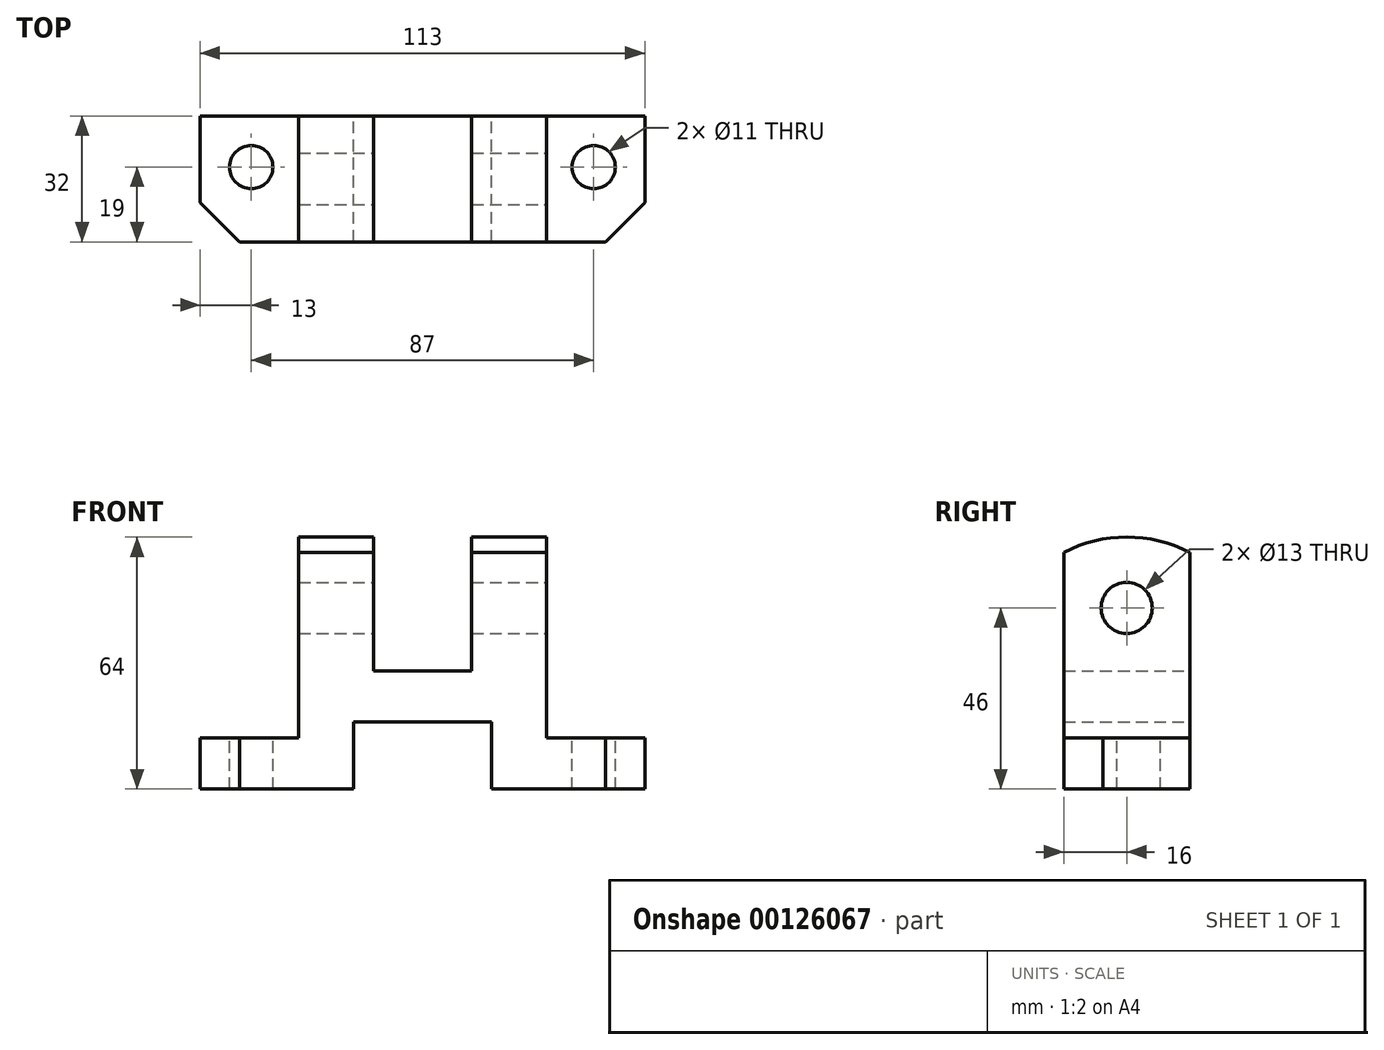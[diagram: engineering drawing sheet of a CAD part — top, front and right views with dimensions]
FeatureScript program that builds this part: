
annotation { "Feature Type Name" : "Feature", "Feature Type Description" : "" }
export const myFeature = defineFeature(function(context is Context, id is Id, definition is map)
    precondition{}
    {
        {
            var Q0;
            Q0=qCreatedBy(makeId("Front.planeOp"),FACE);
            var sketch = newSketch(context, id + "F0", { "sketchPlane" : qUnion([Q0])});
            skLineSegment(sketch, "E0.bottom", {"start": v(0, 0) * mm, "end": v(39, 0) * mm});
            skLineSegment(sketch, "E0.top", {"start": v(25, 64) * mm, "end": v(44, 64) * mm});
            skLineSegment(sketch, "E0.left", {"start": v(0, 0) * mm, "end": v(0, 13) * mm});
            skLineSegment(sketch, "E0.right", {"start": v(113, 0) * mm, "end": v(113, 13) * mm});
            skLineSegment(sketch, "E1.top", {"start": v(39, 17) * mm, "end": v(74, 17) * mm});
            skLineSegment(sketch, "E1.left", {"start": v(39, 0) * mm, "end": v(39, 17) * mm});
            skLineSegment(sketch, "E1.right", {"start": v(74, 0) * mm, "end": v(74, 17) * mm});
            skLineSegment(sketch, "E2.top", {"start": v(44, 30) * mm, "end": v(69, 30) * mm});
            skLineSegment(sketch, "E2.left", {"start": v(44, 64) * mm, "end": v(44, 30) * mm});
            skLineSegment(sketch, "E2.right", {"start": v(69, 64) * mm, "end": v(69, 30) * mm});
            skLineSegment(sketch, "E3.top", {"start": v(88, 13) * mm, "end": v(113, 13) * mm});
            skLineSegment(sketch, "E3.left", {"start": v(88, 64) * mm, "end": v(88, 13) * mm});
            skLineSegment(sketch, "E4.top", {"start": v(25, 13) * mm, "end": v(0, 13) * mm});
            skLineSegment(sketch, "E4.left", {"start": v(25, 64) * mm, "end": v(25, 13) * mm});
            skLineSegment(sketch, "E5.trimOffspring", {"start": v(69, 64) * mm, "end": v(88, 64) * mm});
            skLineSegment(sketch, "E6.trimOffspring", {"start": v(74, 0) * mm, "end": v(113, 0) * mm});
            skSolve(sketch);
        }
        {
            var Q0;
            Q0=makeQuery(id+"F0.imprint","IMPRINT",FACE,{"disambiguationData":[TD([[makeQuery(id+"F0.imprint","IMPRINT",EDGE,{"derivedFrom":sQuery(id+"F0.wireOp",EDGE,"E0.bottom")}),1.0]])]});
            extrude(context, id + "F1", {"entities" : qUnion([Q0]), "endBound" : BoundingType.SYMMETRIC, "depth" : 32 * mm});
        }
        {
            var Q0;
            Q0=makeQuery(id+"F1.opExtrude","SWEPT_FACE",FACE,{"disambiguationData":[OSD([sQuery(id+"F0.wireOp",EDGE,"E3.top")])]});
            var sketch = newSketch(context, id + "F2", { "sketchPlane" : qUnion([Q0])});
            skCircle(sketch, "E7", {"center": v(100, 3) * mm, "radius": 5.5 * mm});
            skCircle(sketch, "E8", {"center": v(13, 3) * mm, "radius": 5.5 * mm});
            skSolve(sketch);
        }
        {
            var Q0;
            Q0=makeQuery(id+"F2.imprint","IMPRINT",FACE,{"disambiguationData":[TD([[makeQuery(id+"F2.imprint","IMPRINT",EDGE,{"derivedFrom":sQuery(id+"F2.wireOp",EDGE,"E7")}),1.0]])]});
            var Q1;
            Q1=makeQuery(id+"F2.imprint","IMPRINT",FACE,{"disambiguationData":[TD([[makeQuery(id+"F2.imprint","IMPRINT",EDGE,{"derivedFrom":sQuery(id+"F2.wireOp",EDGE,"E8")}),1.0]])]});
            extrude(context, id + "F3", {"entities" : qUnion([Q0, Q1]), "operationType" : NewBodyOperationType.REMOVE, "endBound" : BoundingType.THROUGH_ALL, "oppositeDirection" : true, "depth" : 25 * mm});
        }
        {
            var Q0;
            Q0=makeQuery(id+"F1.opExtrude","CAP_EDGE",EDGE,{"disambiguationData":[OSD([sQuery(id+"F0.wireOp",EDGE,"E0.left")])],"isStart":false});
            var Q1;
            Q1=makeQuery(id+"F1.opExtrude","CAP_EDGE",EDGE,{"disambiguationData":[OSD([sQuery(id+"F0.wireOp",EDGE,"E0.right")])],"isStart":false});
            chamfer(context, id + "F4", {"entities" : qUnion([Q0, Q1]), "chamferType" : ChamferType.OFFSET_ANGLE, "width" : 10 * mm, "oppositeDirection" : false, "angle" : 45 * degree, "tangentPropagation" : true});
        }
        {
            var Q0;
            Q0=makeQuery(id+"F1.opExtrude","SWEPT_FACE",FACE,{"disambiguationData":[OSD([sQuery(id+"F0.wireOp",EDGE,"E3.left")])]});
            var sketch = newSketch(context, id + "F5", { "sketchPlane" : qUnion([Q0])});
            skCircle(sketch, "E9", {"center": v(0, 46) * mm, "radius": 6.5 * mm});
            skArc(sketch, "E10", {"start": v(16, 60.13) * mm, "mid": v(0, 64) * mm, "end": v(-16, 60.13) * mm});
            skLineSegment(sketch, "E11.0", {"start": v(-16, 64) * mm, "end": v(16, 64) * mm});
            skLineSegment(sketch, "E12", {"start": v(0, 29) * mm, "end": v(0, 88.27) * mm, "construction": true});
            skPoint(sketch, "E13", {"position": v(0, 64) * mm});
            skSolve(sketch);
        }
        {
            var Q0;
            Q0=makeQuery(id+"F5.imprint","IMPRINT",FACE,{"disambiguationData":[TD([[makeQuery(id+"F5.imprint","IMPRINT",EDGE,{"derivedFrom":sQuery(id+"F5.wireOp",EDGE,"E9")}),1.0]])]});
            var Q1;
            {var subQ0=sQuery(id+"F5.wireOp",EDGE,"E10");var subQ1=makeQuery(id+"F1.opExtrude","CAP_EDGE",EDGE,{"disambiguationData":[OSD([sQuery(id+"F0.wireOp",EDGE,"E3.left")])],"isStart":false});var subQ2=makeQuery(id+"F5.imprint","INTERSECT",VERTEX,{"derivedFrom":[subQ1,subQ0]});Q1=makeQuery(id+"F5.imprint","IMPRINT",FACE,{"disambiguationData":[TD([[makeQuery(id+"F5.imprint","IMPRINT",EDGE,{"disambiguationData":[TD([[subQ2,1.0]])],"derivedFrom":subQ0}),-1.0]])]});}
            var Q2;
            {var subQ0=sQuery(id+"F5.wireOp",EDGE,"E10");var subQ1=makeQuery(id+"F1.opExtrude","CAP_EDGE",EDGE,{"disambiguationData":[OSD([sQuery(id+"F0.wireOp",EDGE,"E3.left")])],"isStart":true});var subQ2=makeQuery(id+"F5.imprint","INTERSECT",VERTEX,{"derivedFrom":[subQ1,subQ0]});Q2=makeQuery(id+"F5.imprint","IMPRINT",FACE,{"disambiguationData":[TD([[makeQuery(id+"F5.imprint","IMPRINT",EDGE,{"disambiguationData":[TD([[subQ2,-1.0]])],"derivedFrom":subQ0}),-1.0]])]});}
            extrude(context, id + "F6", {"entities" : qUnion([Q0, Q1, Q2]), "operationType" : NewBodyOperationType.REMOVE, "endBound" : BoundingType.THROUGH_ALL, "oppositeDirection" : true, "depth" : 25 * mm});
        }
    });
